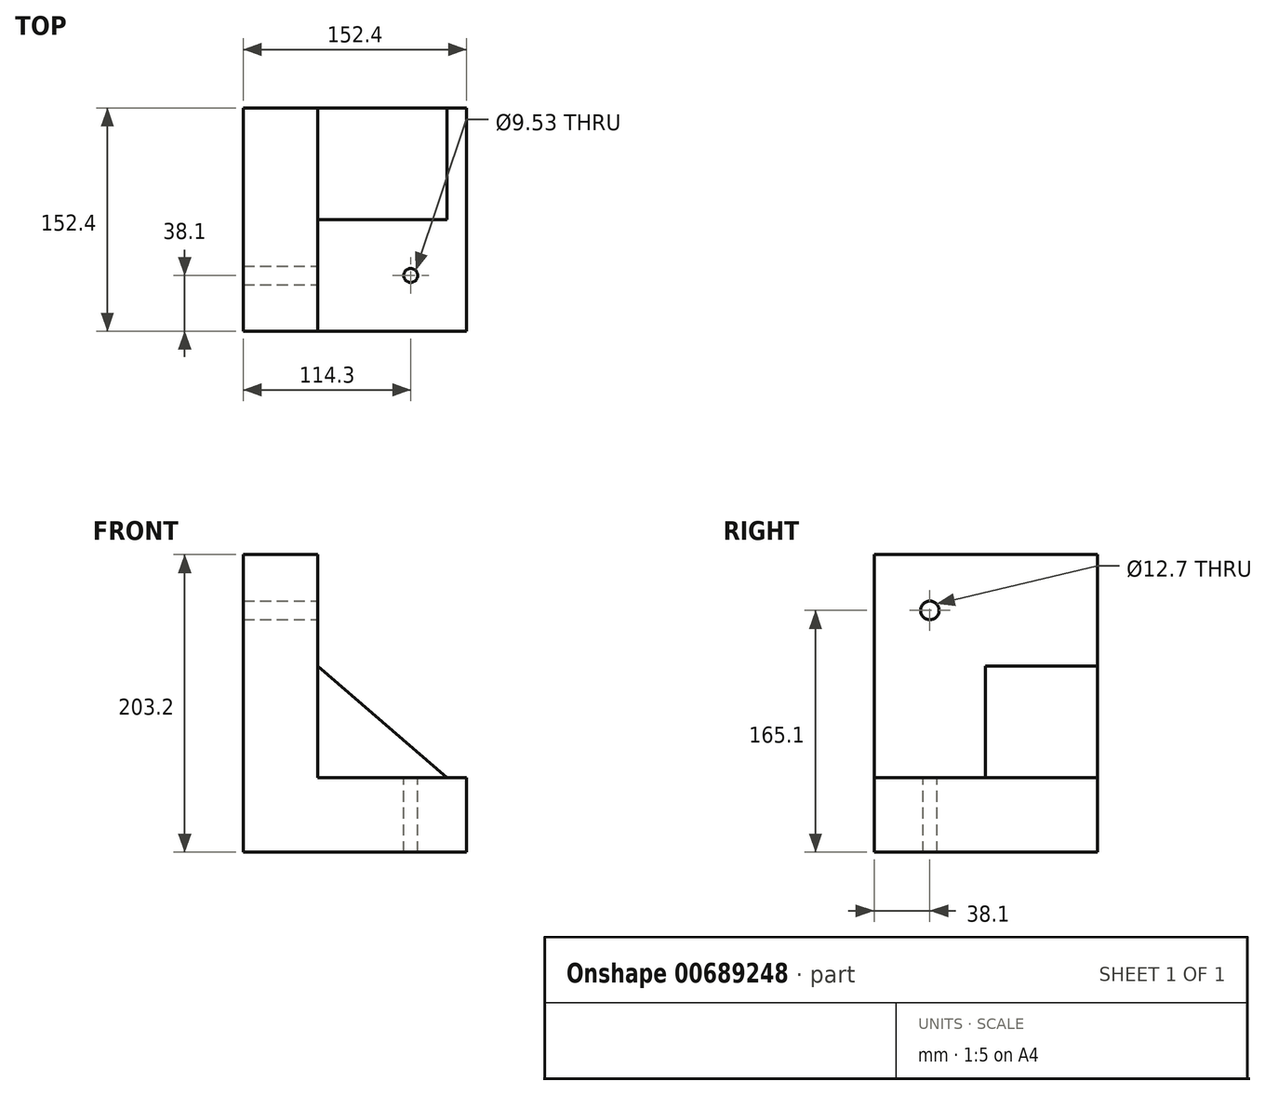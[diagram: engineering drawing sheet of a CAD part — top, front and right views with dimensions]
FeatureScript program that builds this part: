
annotation { "Feature Type Name" : "Feature", "Feature Type Description" : "" }
export const myFeature = defineFeature(function(context is Context, id is Id, definition is map)
    precondition{}
    {
        {
            var Q0;
            Q0=qCreatedBy(makeId("Front.planeOp"),FACE);
            var sketch = newSketch(context, id + "F0", { "sketchPlane" : qUnion([Q0])});
            skLineSegment(sketch, "E0", {"start": v(13.44, 173.4) * mm, "end": v(-37.36, 173.4) * mm});
            skLineSegment(sketch, "E1", {"start": v(-37.36, 173.4) * mm, "end": v(-37.36, -29.8) * mm});
            skLineSegment(sketch, "E2", {"start": v(-37.36, -29.8) * mm, "end": v(115.04, -29.8) * mm});
            skLineSegment(sketch, "E3", {"start": v(115.04, -29.8) * mm, "end": v(115.04, 21) * mm});
            skLineSegment(sketch, "E4", {"start": v(13.44, 21) * mm, "end": v(115.04, 21) * mm});
            skLineSegment(sketch, "E5", {"start": v(13.44, 173.4) * mm, "end": v(13.44, 21) * mm});
            skSolve(sketch);
        }
        {
            var Q0;
            Q0 = qSketchRegion(id + "F0", true);
            extrude(context, id + "F1", {"entities" : qUnion([Q0]), "depth" : 152.4 * mm, "offsetDistance" : 25.4 * mm});
        }
        {
            var Q0;
            Q0=makeQuery(id+"F1.opExtrude","SWEPT_FACE",FACE,{"disambiguationData":[OSD([sQuery(id+"F0.wireOp",EDGE,"E4")])]});
            var sketch = newSketch(context, id + "F2", { "sketchPlane" : qUnion([Q0])});
            skLineSegment(sketch, "E6.bottom", {"start": v(0, 0) * mm, "end": v(101.6, 0) * mm});
            skLineSegment(sketch, "E6.top", {"start": v(0, -76.2) * mm, "end": v(101.6, -76.2) * mm});
            skLineSegment(sketch, "E6.left", {"start": v(0, 0) * mm, "end": v(0, -76.2) * mm});
            skLineSegment(sketch, "E6.right", {"start": v(101.6, 0) * mm, "end": v(101.6, -76.2) * mm});
            skSolve(sketch);
        }
        {
            var Q0;
            Q0 = qSketchRegion(id + "F2", true);
            extrude(context, id + "F3", {"entities" : qUnion([Q0]), "operationType" : NewBodyOperationType.ADD, "depth" : 76.2 * mm, "offsetDistance" : 25.4 * mm});
        }
        {
            var Q0;
            Q0=makeQuery(id+"F3.opExtrude","SWEPT_FACE",FACE,{"disambiguationData":[OSD([sQuery(id+"F2.wireOp",EDGE,"E6.top")])]});
            var sketch = newSketch(context, id + "F4", { "sketchPlane" : qUnion([Q0])});
            skLineSegment(sketch, "E7", {"start": v(13.44, 97.2) * mm, "end": v(101.6, 21) * mm});
            skLineSegment(sketch, "E8", {"start": v(13.44, 97.2) * mm, "end": v(101.6, 97.2) * mm});
            skLineSegment(sketch, "E9", {"start": v(101.6, 97.2) * mm, "end": v(101.6, 21) * mm});
            skSolve(sketch);
        }
        {
            var Q0;
            Q0 = qSketchRegion(id + "F4", true);
            extrude(context, id + "F5", {"entities" : qUnion([Q0]), "operationType" : NewBodyOperationType.REMOVE, "oppositeDirection" : true, "depth" : 76.2 * mm, "offsetDistance" : 25.4 * mm});
        }
        {
            var Q0;
            Q0=makeQuery(id+"F1.opExtrude","SWEPT_FACE",FACE,{"disambiguationData":[OSD([sQuery(id+"F0.wireOp",EDGE,"E4")])]});
            var sketch = newSketch(context, id + "F6", { "sketchPlane" : qUnion([Q0])});
            skCircle(sketch, "E10", {"center": v(76.94, -114.3) * mm, "radius": 4.76 * mm});
            skSolve(sketch);
        }
        {
            var Q0;
            Q0=sQuery(id+"F6.wireOp",VERTEX,"E10.center");
            var Q1;
            Q1=makeQuery(id+"F1.opExtrude","SWEPT_BODY",BODY,{"disambiguationData":[OSD([sQuery(id+"F0.wireOp",EDGE,"E0"),sQuery(id+"F0.wireOp",EDGE,"E1"),sQuery(id+"F0.wireOp",EDGE,"E2"),sQuery(id+"F0.wireOp",EDGE,"E3"),sQuery(id+"F0.wireOp",EDGE,"E4"),sQuery(id+"F0.wireOp",EDGE,"E5")])]});
            hole(context, id + "F7", {"style" : HoleStyle.SIMPLE, "endStyle" : HoleEndStyle.THROUGH, "holeDiameter" : 9.52 * mm, "majorDiameter" : 6.35 * mm, "isTappedThrough" : true, "tappedDepth" : 12.7 * mm, "tapClearance" : 3, "locations" : qUnion([Q0]), "scope" : qUnion([Q1])});
        }
        {
            var Q0;
            Q0=makeQuery(id+"F1.opExtrude","SWEPT_FACE",FACE,{"disambiguationData":[OSD([sQuery(id+"F0.wireOp",EDGE,"E5")])]});
            var sketch = newSketch(context, id + "F8", { "sketchPlane" : qUnion([Q0])});
            skPoint(sketch, "E11", {"position": v(-114.3, 135.3) * mm});
            skSolve(sketch);
        }
        {
            var Q0;
            Q0=sQuery(id+"F8.wireOp",VERTEX,"E11");
            var Q1;
            Q1=makeQuery(id+"F1.opExtrude","SWEPT_BODY",BODY,{"disambiguationData":[OSD([sQuery(id+"F0.wireOp",EDGE,"E0"),sQuery(id+"F0.wireOp",EDGE,"E1"),sQuery(id+"F0.wireOp",EDGE,"E2"),sQuery(id+"F0.wireOp",EDGE,"E3"),sQuery(id+"F0.wireOp",EDGE,"E4"),sQuery(id+"F0.wireOp",EDGE,"E5")])]});
            hole(context, id + "F9", {"style" : HoleStyle.SIMPLE, "endStyle" : HoleEndStyle.THROUGH, "holeDiameter" : 12.7 * mm, "majorDiameter" : 6.35 * mm, "isTappedThrough" : true, "tappedDepth" : 12.7 * mm, "tapClearance" : 3, "locations" : qUnion([Q0]), "scope" : qUnion([Q1])});
        }
    });
